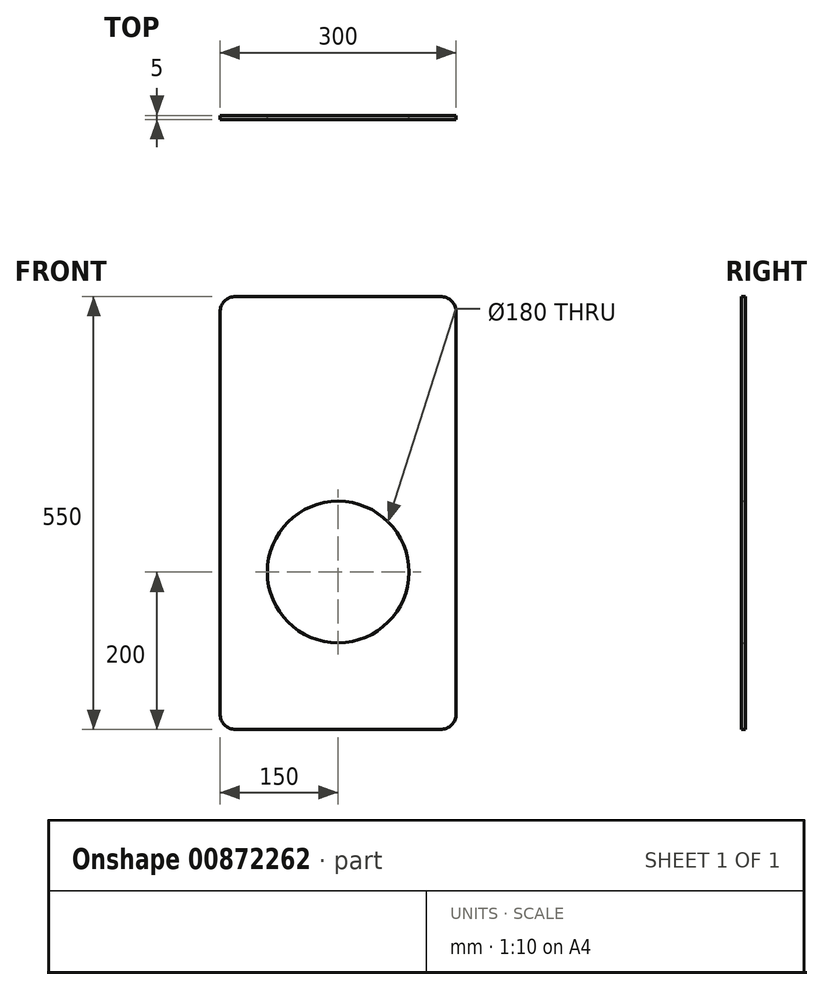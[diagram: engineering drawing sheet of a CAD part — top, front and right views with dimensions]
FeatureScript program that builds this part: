
annotation { "Feature Type Name" : "Feature", "Feature Type Description" : "" }
export const myFeature = defineFeature(function(context is Context, id is Id, definition is map)
    precondition{}
    {
        {
            var Q0;
            Q0=qCreatedBy(makeId("Front.planeOp"),FACE);
            var sketch = newSketch(context, id + "F0", { "sketchPlane" : qUnion([Q0])});
            skLineSegment(sketch, "E0.bottom", {"start": v(-130, 275) * mm, "end": v(130, 275) * mm});
            skLineSegment(sketch, "E0.top", {"start": v(-130, -275) * mm, "end": v(130, -275) * mm});
            skLineSegment(sketch, "E0.left", {"start": v(-150, 255) * mm, "end": v(-150, -255) * mm});
            skLineSegment(sketch, "E0.right", {"start": v(150, 255) * mm, "end": v(150, -255) * mm});
            skPoint(sketch, "E0.middle", {"position": v(0, 0) * mm});
            skPoint(sketch, "E1.visualSharp", {"position": v(-150, 275) * mm});
            skArc(sketch, "E1.filletArc", {"start": v(-130, 275) * mm, "mid": v(-144.14, 269.14) * mm, "end": v(-150, 255) * mm});
            skPoint(sketch, "E2.visualSharp", {"position": v(150, 275) * mm});
            skArc(sketch, "E2.filletArc", {"start": v(150, 255) * mm, "mid": v(144.14, 269.14) * mm, "end": v(130, 275) * mm});
            skPoint(sketch, "E3.visualSharp", {"position": v(-150, -275) * mm});
            skArc(sketch, "E3.filletArc", {"start": v(-150, -255) * mm, "mid": v(-144.14, -269.14) * mm, "end": v(-130, -275) * mm});
            skPoint(sketch, "E4.visualSharp", {"position": v(150, -275) * mm});
            skArc(sketch, "E4.filletArc", {"start": v(130, -275) * mm, "mid": v(144.14, -269.14) * mm, "end": v(150, -255) * mm});
            skLineSegment(sketch, "E5", {"start": v(-202.7, -75) * mm, "end": v(285.2, -75) * mm, "construction": true});
            skLineSegment(sketch, "E6", {"start": v(0, 113.08) * mm, "end": v(0, -216.92) * mm, "construction": true});
            skCircle(sketch, "E7", {"center": v(0, -75) * mm, "radius": 90 * mm});
            skSolve(sketch);
        }
        {
            var Q0;
            Q0=makeQuery(id+"F0.imprint","IMPRINT",FACE,{"disambiguationData":[TD([[makeQuery(id+"F0.imprint","IMPRINT",EDGE,{"derivedFrom":sQuery(id+"F0.wireOp",EDGE,"E0.bottom")}),-1.0]])]});
            extrude(context, id + "F1", {"entities" : qUnion([Q0]), "endBound" : BoundingType.SYMMETRIC, "depth" : 5 * mm, "offsetDistance" : 25 * mm});
        }
    });
